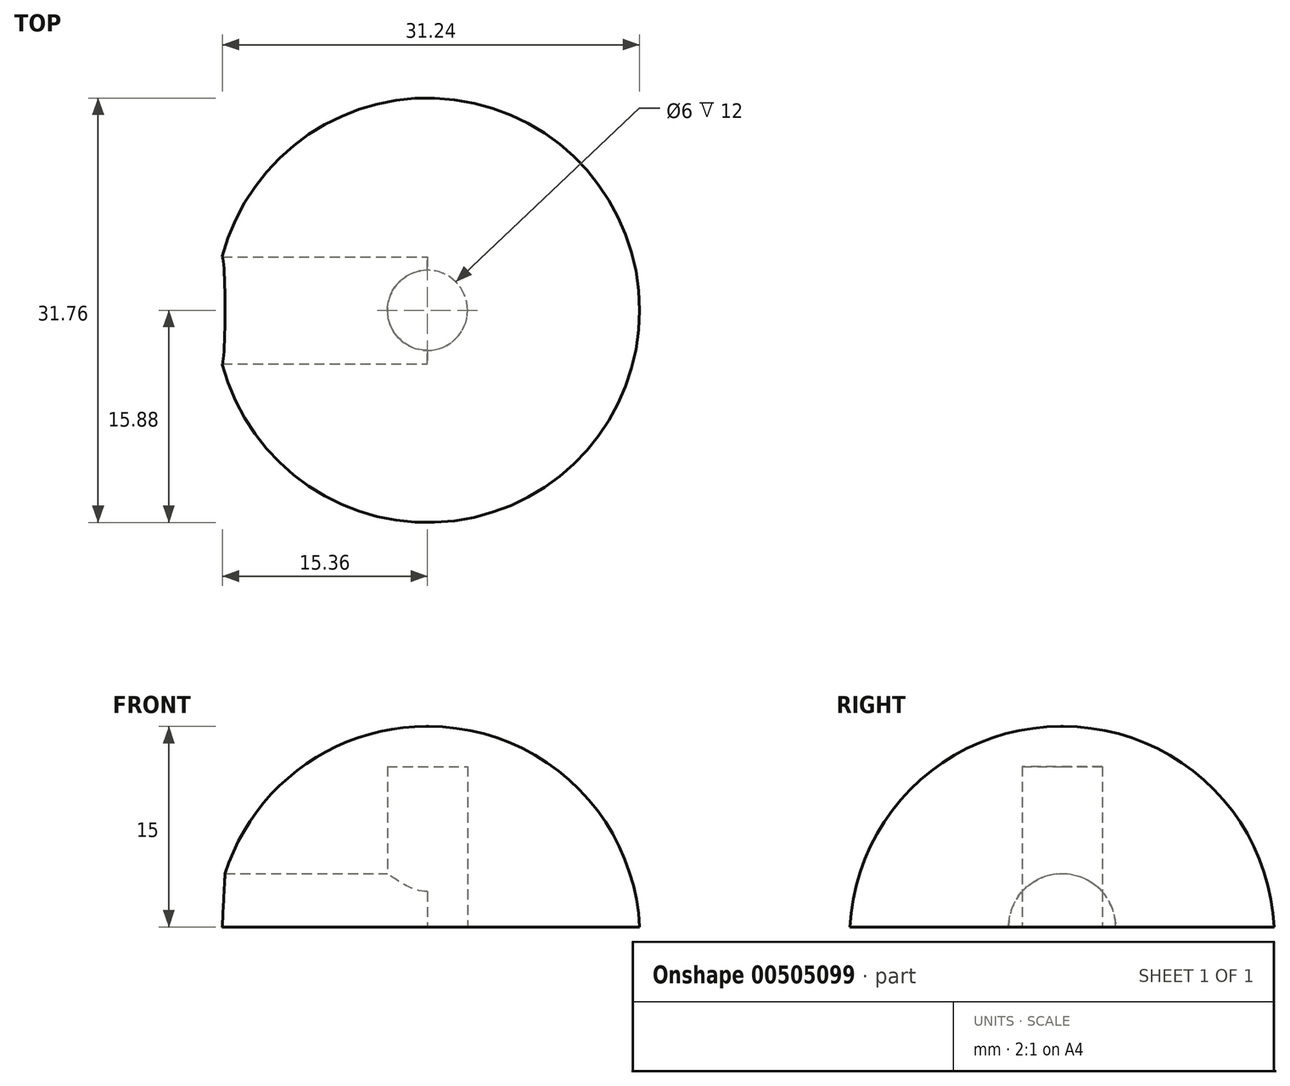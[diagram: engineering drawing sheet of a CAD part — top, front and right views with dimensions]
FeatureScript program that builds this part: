
annotation { "Feature Type Name" : "Feature", "Feature Type Description" : "" }
export const myFeature = defineFeature(function(context is Context, id is Id, definition is map)
    precondition{}
    {
        {
            var Q0;
            Q0=qCreatedBy(makeId("Top.planeOp"),FACE);
            var sketch = newSketch(context, id + "F0", { "sketchPlane" : qUnion([Q0])});
            skCircle(sketch, "E0", {"center": v(0, 0) * mm, "radius": 15.88 * mm});
            skSolve(sketch);
        }
        {
            var Q0;
            Q0 = qSketchRegion(id + "F0", true);
            extrude(context, id + "F1", {"entities" : qUnion([Q0]), "depth" : 15 * mm});
        }
        {
            var Q0;
            Q0=makeQuery(id+"F1.opExtrude","CAP_EDGE",EDGE,{"disambiguationData":[OSD([sQuery(id+"F0.wireOp",EDGE,"E0")])],"isStart":false});
            fillet(context, id + "F2", {"entities" : qUnion([Q0]), "radius" : 15.8 * mm, "tangentPropagation" : true, "allowEdgeOverflow" : false});
        }
        {
            var Q0;
            Q0=makeQuery(id+"F1.opExtrude","CAP_FACE",FACE,{"disambiguationData":[OSD([sQuery(id+"F0.wireOp",EDGE,"E0")])],"isStart":true});
            var sketch = newSketch(context, id + "F3", { "sketchPlane" : qUnion([Q0])});
            skCircle(sketch, "E1", {"center": v(0, 0) * mm, "radius": 3 * mm});
            skSolve(sketch);
        }
        {
            var Q0;
            Q0=makeQuery(id+"F3.imprint","IMPRINT",FACE,{"disambiguationData":[TD([[makeQuery(id+"F3.imprint","IMPRINT",EDGE,{"derivedFrom":sQuery(id+"F3.wireOp",EDGE,"E1")}),1.0]])]});
            extrude(context, id + "F4", {"entities" : qUnion([Q0]), "operationType" : NewBodyOperationType.REMOVE, "oppositeDirection" : true, "depth" : 12 * mm, "offsetDistance" : 25 * mm});
        }
        {
            var Q0;
            Q0=qCreatedBy(makeId("Right.planeOp"),FACE);
            var sketch = newSketch(context, id + "F5", { "sketchPlane" : qUnion([Q0])});
            skCircle(sketch, "E2", {"center": v(0, 0) * mm, "radius": 4 * mm});
            skSolve(sketch);
        }
        {
            var Q0;
            Q0 = qSketchRegion(id + "F5", true);
            extrude(context, id + "F6", {"entities" : qUnion([Q0]), "operationType" : NewBodyOperationType.REMOVE, "oppositeDirection" : true, "depth" : 25 * mm});
        }
    });
